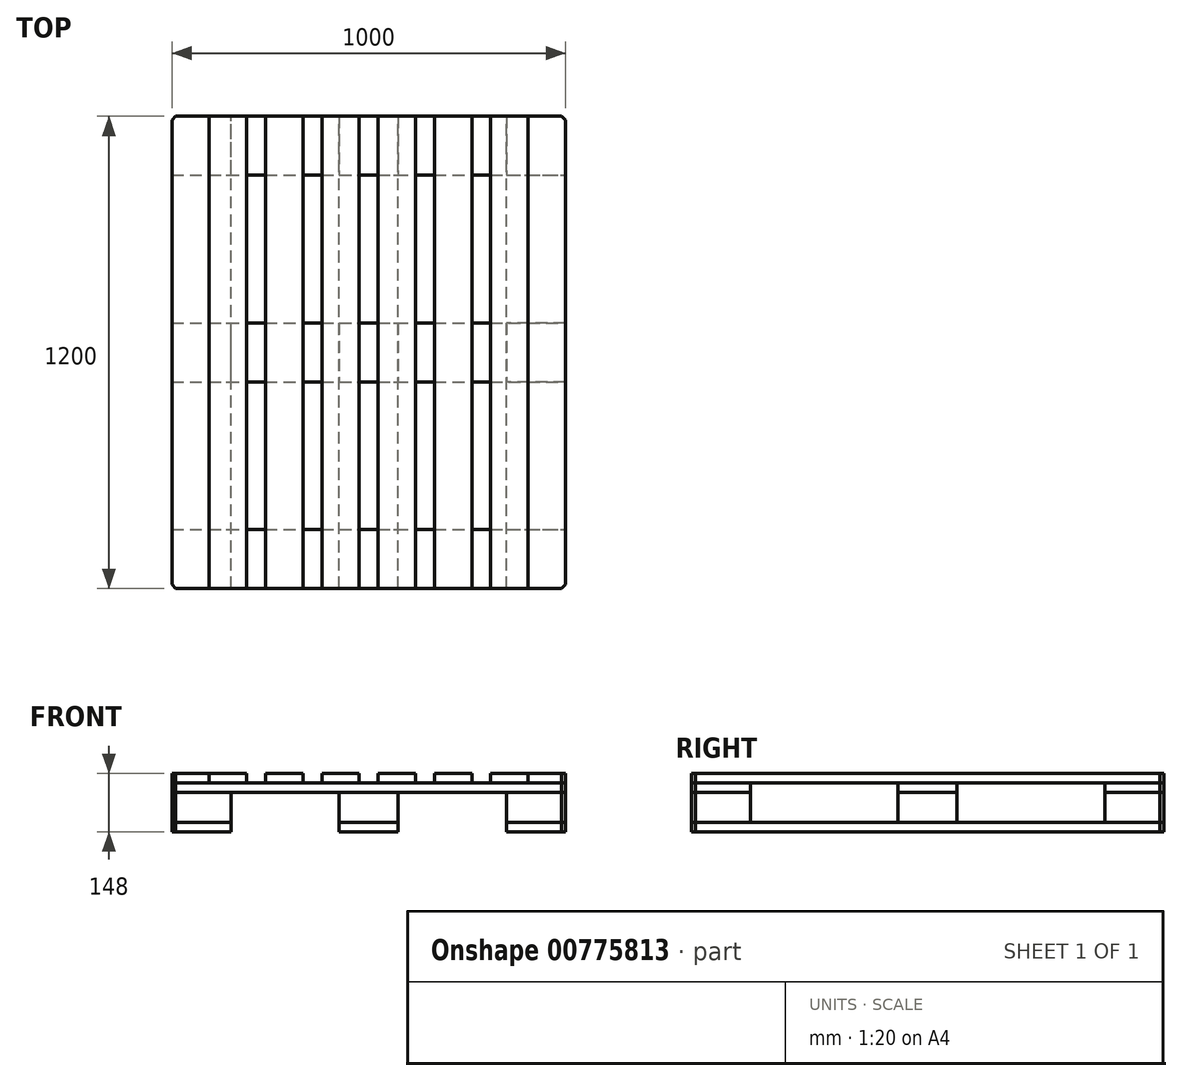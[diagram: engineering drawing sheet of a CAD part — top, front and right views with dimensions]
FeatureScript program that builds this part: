
annotation { "Feature Type Name" : "Feature", "Feature Type Description" : "" }
export const myFeature = defineFeature(function(context is Context, id is Id, definition is map)
    precondition{}
    {
        {
            var Q0;
            Q0=qCreatedBy(makeId("Top.planeOp"),FACE);
            var sketch = newSketch(context, id + "F0", { "sketchPlane" : qUnion([Q0])});
            skLineSegment(sketch, "E0.bottom", {"start": v(0, 0) * mm, "end": v(95, 0) * mm});
            skLineSegment(sketch, "E0.top", {"start": v(0, 1200) * mm, "end": v(95, 1200) * mm});
            skLineSegment(sketch, "E0.left", {"start": v(0, 0) * mm, "end": v(0, 1200) * mm});
            skLineSegment(sketch, "E0.right", {"start": v(95, 0) * mm, "end": v(95, 1200) * mm});
            skLineSegment(sketch, "E1.bottom", {"start": v(238, 0) * mm, "end": v(333, 0) * mm});
            skLineSegment(sketch, "E1.top", {"start": v(238, 1200) * mm, "end": v(333, 1200) * mm});
            skLineSegment(sketch, "E1.left", {"start": v(238, 0) * mm, "end": v(238, 1200) * mm});
            skLineSegment(sketch, "E1.right", {"start": v(333, 0) * mm, "end": v(333, 1200) * mm});
            skLineSegment(sketch, "E2.bottom", {"start": v(381, 0) * mm, "end": v(476, 0) * mm});
            skLineSegment(sketch, "E2.top", {"start": v(381, 1200) * mm, "end": v(476, 1200) * mm});
            skLineSegment(sketch, "E2.left", {"start": v(381, 0) * mm, "end": v(381, 1200) * mm});
            skLineSegment(sketch, "E2.right", {"start": v(476, 0) * mm, "end": v(476, 1200) * mm});
            skLineSegment(sketch, "E3.bottom", {"start": v(524, 0) * mm, "end": v(619, 0) * mm});
            skLineSegment(sketch, "E3.top", {"start": v(524, 1200) * mm, "end": v(619, 1200) * mm});
            skLineSegment(sketch, "E3.left", {"start": v(524, 0) * mm, "end": v(524, 1200) * mm});
            skLineSegment(sketch, "E3.right", {"start": v(619, 0) * mm, "end": v(619, 1200) * mm});
            skLineSegment(sketch, "E4.bottom", {"start": v(667, 0) * mm, "end": v(762, 0) * mm});
            skLineSegment(sketch, "E4.top", {"start": v(667, 1200) * mm, "end": v(762, 1200) * mm});
            skLineSegment(sketch, "E4.left", {"start": v(667, 0) * mm, "end": v(667, 1200) * mm});
            skLineSegment(sketch, "E4.right", {"start": v(762, 0) * mm, "end": v(762, 1200) * mm});
            skLineSegment(sketch, "E5.bottom", {"start": v(905, 0) * mm, "end": v(1000, 0) * mm});
            skLineSegment(sketch, "E5.top", {"start": v(905, 1200) * mm, "end": v(1000, 1200) * mm});
            skLineSegment(sketch, "E5.left", {"start": v(905, 0) * mm, "end": v(905, 1200) * mm});
            skLineSegment(sketch, "E5.right", {"start": v(1000, 0) * mm, "end": v(1000, 1200) * mm});
            skLineSegment(sketch, "E6.bottom", {"start": v(95.1, 0) * mm, "end": v(190, 0) * mm});
            skLineSegment(sketch, "E6.top", {"start": v(95.1, 1200) * mm, "end": v(190, 1200) * mm});
            skLineSegment(sketch, "E6.left", {"start": v(95.1, 0) * mm, "end": v(95.1, 1200) * mm});
            skLineSegment(sketch, "E6.right", {"start": v(190, 0) * mm, "end": v(190, 1200) * mm});
            skLineSegment(sketch, "E7.bottom", {"start": v(904.9, 0) * mm, "end": v(810, 0) * mm});
            skLineSegment(sketch, "E7.top", {"start": v(904.9, 1200) * mm, "end": v(810, 1200) * mm});
            skLineSegment(sketch, "E7.left", {"start": v(904.9, 0) * mm, "end": v(904.9, 1200) * mm});
            skLineSegment(sketch, "E7.right", {"start": v(810, 0) * mm, "end": v(810, 1200) * mm});
            skLineSegment(sketch, "E8", {"start": v(-393.77, 0) * mm, "end": v(-393.77, 800) * mm});
            skLineSegment(sketch, "E9", {"start": v(-393.77, 800) * mm, "end": v(1315.18, 800) * mm});
            skSolve(sketch);
        }
        {
            var Q0;
            Q0 = qSketchRegion(id + "F0", true);
            extrude(context, id + "F1", {"entities" : qUnion([Q0]), "depth" : 24 * mm, "offsetDistance" : 25 * mm});
        }
        {
            var Q0;
            Q0=qCreatedBy(makeId("Top.planeOp"),FACE);
            var sketch = newSketch(context, id + "F2", { "sketchPlane" : qUnion([Q0])});
            skLineSegment(sketch, "E10.bottom", {"start": v(0, 0) * mm, "end": v(1000, 0) * mm});
            skLineSegment(sketch, "E10.top", {"start": v(0, 150) * mm, "end": v(1000, 150) * mm});
            skLineSegment(sketch, "E10.left", {"start": v(0, 0) * mm, "end": v(0, 150) * mm});
            skLineSegment(sketch, "E10.right", {"start": v(1000, 0) * mm, "end": v(1000, 150) * mm});
            skLineSegment(sketch, "E11.bottom", {"start": v(0, 525) * mm, "end": v(1000, 525) * mm});
            skLineSegment(sketch, "E11.top", {"start": v(0, 675) * mm, "end": v(1000, 675) * mm});
            skLineSegment(sketch, "E11.left", {"start": v(0, 525) * mm, "end": v(0, 675) * mm});
            skLineSegment(sketch, "E11.right", {"start": v(1000, 525) * mm, "end": v(1000, 675) * mm});
            skLineSegment(sketch, "E12.bottom", {"start": v(0, 1050) * mm, "end": v(1000, 1050) * mm});
            skLineSegment(sketch, "E12.top", {"start": v(0, 1200) * mm, "end": v(1000, 1200) * mm});
            skLineSegment(sketch, "E12.left", {"start": v(0, 1050) * mm, "end": v(0, 1200) * mm});
            skLineSegment(sketch, "E12.right", {"start": v(1000, 1050) * mm, "end": v(1000, 1200) * mm});
            skSolve(sketch);
        }
        {
            var Q0;
            Q0 = qSketchRegion(id + "F2", true);
            extrude(context, id + "F3", {"entities" : qUnion([Q0]), "oppositeDirection" : true, "depth" : 24 * mm, "offsetDistance" : 25 * mm});
        }
        {
            var Q0;
            Q0=qCreatedBy(makeId("Top.planeOp"),FACE);
            var Q1;
            Q1 = qBodyType(qCreatedBy(id + "F5" ,EDGE), BodyType.WIRE);
            cPlane(context, id + "F4", {"entities" : qUnion([Q0, Q1]), "cplaneType" : CPlaneType.OFFSET, "offset" : 24 * mm, "oppositeDirection" : true, "width" : 150 * mm, "height" : 150 * mm});
        }
        {
            var Q0;
            Q0=qCreatedBy(id+"F4.planeOp",FACE);
            var sketch = newSketch(context, id + "F5", { "sketchPlane" : qUnion([Q0])});
            skLineSegment(sketch, "E13.bottom", {"start": v(0, 0) * mm, "end": v(150, 0) * mm});
            skLineSegment(sketch, "E13.top", {"start": v(0, 150) * mm, "end": v(150, 150) * mm});
            skLineSegment(sketch, "E13.left", {"start": v(0, 0) * mm, "end": v(0, 150) * mm});
            skLineSegment(sketch, "E13.right", {"start": v(150, 0) * mm, "end": v(150, 150) * mm});
            skLineSegment(sketch, "E14.bottom", {"start": v(0, 525) * mm, "end": v(150, 525) * mm});
            skLineSegment(sketch, "E14.top", {"start": v(0, 675) * mm, "end": v(150, 675) * mm});
            skLineSegment(sketch, "E14.left", {"start": v(0, 525) * mm, "end": v(0, 675) * mm});
            skLineSegment(sketch, "E14.right", {"start": v(150, 525) * mm, "end": v(150, 675) * mm});
            skLineSegment(sketch, "E15.bottom", {"start": v(0, 1050) * mm, "end": v(150, 1050) * mm});
            skLineSegment(sketch, "E15.top", {"start": v(0, 1200) * mm, "end": v(150, 1200) * mm});
            skLineSegment(sketch, "E15.left", {"start": v(0, 1050) * mm, "end": v(0, 1200) * mm});
            skLineSegment(sketch, "E15.right", {"start": v(150, 1050) * mm, "end": v(150, 1200) * mm});
            skLineSegment(sketch, "E16.bottom", {"start": v(425, 0) * mm, "end": v(575, 0) * mm});
            skLineSegment(sketch, "E16.top", {"start": v(425, 150) * mm, "end": v(575, 150) * mm});
            skLineSegment(sketch, "E16.left", {"start": v(425, 0) * mm, "end": v(425, 150) * mm});
            skLineSegment(sketch, "E16.right", {"start": v(575, 0) * mm, "end": v(575, 150) * mm});
            skLineSegment(sketch, "E17.bottom", {"start": v(425, 1200) * mm, "end": v(575, 1200) * mm});
            skLineSegment(sketch, "E17.top", {"start": v(425, 1050) * mm, "end": v(575, 1050) * mm});
            skLineSegment(sketch, "E17.left", {"start": v(425, 1200) * mm, "end": v(425, 1050) * mm});
            skLineSegment(sketch, "E17.right", {"start": v(575, 1200) * mm, "end": v(575, 1050) * mm});
            skLineSegment(sketch, "E18.bottom", {"start": v(850, 0) * mm, "end": v(1000, 0) * mm});
            skLineSegment(sketch, "E18.top", {"start": v(850, 150) * mm, "end": v(1000, 150) * mm});
            skLineSegment(sketch, "E18.left", {"start": v(850, 0) * mm, "end": v(850, 150) * mm});
            skLineSegment(sketch, "E18.right", {"start": v(1000, 0) * mm, "end": v(1000, 150) * mm});
            skLineSegment(sketch, "E19.bottom", {"start": v(850, 1200) * mm, "end": v(1000, 1200) * mm});
            skLineSegment(sketch, "E19.top", {"start": v(850, 1050) * mm, "end": v(1000, 1050) * mm});
            skLineSegment(sketch, "E19.left", {"start": v(850, 1200) * mm, "end": v(850, 1050) * mm});
            skLineSegment(sketch, "E19.right", {"start": v(1000, 1200) * mm, "end": v(1000, 1050) * mm});
            skLineSegment(sketch, "E20.bottom", {"start": v(1000, 675) * mm, "end": v(850, 675) * mm});
            skLineSegment(sketch, "E20.top", {"start": v(1000, 525) * mm, "end": v(850, 525) * mm});
            skLineSegment(sketch, "E20.left", {"start": v(1000, 675) * mm, "end": v(1000, 525) * mm});
            skLineSegment(sketch, "E20.right", {"start": v(850, 675) * mm, "end": v(850, 525) * mm});
            skLineSegment(sketch, "E21.bottom", {"start": v(425, 675) * mm, "end": v(575, 675) * mm});
            skLineSegment(sketch, "E21.top", {"start": v(425, 525) * mm, "end": v(575, 525) * mm});
            skLineSegment(sketch, "E21.left", {"start": v(425, 675) * mm, "end": v(425, 525) * mm});
            skLineSegment(sketch, "E21.right", {"start": v(575, 675) * mm, "end": v(575, 525) * mm});
            skSolve(sketch);
        }
        {
            var Q0;
            Q0 = qSketchRegion(id + "F5", true);
            extrude(context, id + "F6", {"entities" : qUnion([Q0]), "oppositeDirection" : true, "depth" : 76 * mm, "offsetDistance" : 25 * mm});
        }
        {
            var Q0;
            Q0=qCreatedBy(makeId("Top.planeOp"),FACE);
            cPlane(context, id + "F7", {"entities" : qUnion([Q0]), "cplaneType" : CPlaneType.OFFSET, "offset" : 100 * mm, "oppositeDirection" : true, "width" : 150 * mm, "height" : 150 * mm});
        }
        {
            var Q0;
            Q0=qCreatedBy(id+"F7.planeOp",FACE);
            var sketch = newSketch(context, id + "F8", { "sketchPlane" : qUnion([Q0])});
            skLineSegment(sketch, "E22.bottom", {"start": v(0, 0) * mm, "end": v(150, 0) * mm});
            skLineSegment(sketch, "E22.top", {"start": v(0, 1200) * mm, "end": v(150, 1200) * mm});
            skLineSegment(sketch, "E22.left", {"start": v(0, 0) * mm, "end": v(0, 1200) * mm});
            skLineSegment(sketch, "E22.right", {"start": v(150, 0) * mm, "end": v(150, 1200) * mm});
            skLineSegment(sketch, "E23.bottom", {"start": v(425, 0) * mm, "end": v(575, 0) * mm});
            skLineSegment(sketch, "E23.top", {"start": v(425, 1200) * mm, "end": v(575, 1200) * mm});
            skLineSegment(sketch, "E23.left", {"start": v(425, 0) * mm, "end": v(425, 1200) * mm});
            skLineSegment(sketch, "E23.right", {"start": v(575, 0) * mm, "end": v(575, 1200) * mm});
            skLineSegment(sketch, "E24.bottom", {"start": v(850, 0) * mm, "end": v(1000, 0) * mm});
            skLineSegment(sketch, "E24.top", {"start": v(850, 1200) * mm, "end": v(1000, 1200) * mm});
            skLineSegment(sketch, "E24.left", {"start": v(850, 0) * mm, "end": v(850, 1200) * mm});
            skLineSegment(sketch, "E24.right", {"start": v(1000, 0) * mm, "end": v(1000, 1200) * mm});
            skSolve(sketch);
        }
        {
            var Q0;
            Q0=makeQuery(id+"F8.imprint","IMPRINT",FACE,{"disambiguationData":[TD([[makeQuery(id+"F8.imprint","IMPRINT",EDGE,{"derivedFrom":sQuery(id+"F8.wireOp",EDGE,"EczPgE0n-K9yp-B3PO-EOS9-lX0zIsuZnhOC.bottom")}),1.0]])]});
            var Q1;
            Q1=makeQuery(id+"F8.imprint","IMPRINT",FACE,{"disambiguationData":[TD([[makeQuery(id+"F8.imprint","IMPRINT",EDGE,{"derivedFrom":sQuery(id+"F8.wireOp",EDGE,"n37sNpmZ-Vokc-glh2-zaN3-OXUCp4wZ9gNM.bottom")}),-1.0]])]});
            var Q2;
            Q2=makeQuery(id+"F8.imprint","IMPRINT",FACE,{"disambiguationData":[TD([[makeQuery(id+"F8.imprint","IMPRINT",EDGE,{"derivedFrom":sQuery(id+"F8.wireOp",EDGE,"Ks7QyBSp-k5Ov-2m7H-Jzkb-e3JOm2grHWz5.bottom")}),1.0]])]});
            var Q3;
            Q3=makeQuery(id+"F8.imprint","IMPRINT",FACE,{"disambiguationData":[TD([[makeQuery(id+"F8.imprint","IMPRINT",EDGE,{"derivedFrom":sQuery(id+"F8.wireOp",EDGE,"ck5NWcSz-vigR-tb6p-G7Lp-A0RWy0raUwrF.bottom")}),-1.0]])]});
            var Q4;
            Q4=makeQuery(id+"F8.imprint","IMPRINT",FACE,{"disambiguationData":[TD([[makeQuery(id+"F8.imprint","IMPRINT",EDGE,{"derivedFrom":sQuery(id+"F8.wireOp",EDGE,"sv6O0ENj-LKTy-FbcM-Dksy-kAM6wW1Upfch.bottom")}),1.0]])]});
            var Q5;
            Q5=makeQuery(id+"F8.imprint","IMPRINT",FACE,{"disambiguationData":[TD([[makeQuery(id+"F8.imprint","IMPRINT",EDGE,{"derivedFrom":sQuery(id+"F8.wireOp",EDGE,"OLO49vYj-GmuG-Gr7v-j1kl-gfgOTdw78I8l.bottom")}),-1.0]])]});
            var Q6;
            Q6=makeQuery(id+"F8.imprint","IMPRINT",FACE,{"disambiguationData":[TD([[makeQuery(id+"F8.imprint","IMPRINT",EDGE,{"derivedFrom":sQuery(id+"F8.wireOp",EDGE,"tdcu3QGg-uwbD-OHdg-jPnv-YvNIwUOHGk3V.bottom")}),1.0]])]});
            var Q7;
            Q7=makeQuery(id+"F8.imprint","IMPRINT",FACE,{"disambiguationData":[TD([[makeQuery(id+"F8.imprint","IMPRINT",EDGE,{"derivedFrom":sQuery(id+"F8.wireOp",EDGE,"E22.bottom")}),1.0]])]});
            var Q8;
            Q8=makeQuery(id+"F8.imprint","IMPRINT",FACE,{"disambiguationData":[TD([[makeQuery(id+"F8.imprint","IMPRINT",EDGE,{"derivedFrom":sQuery(id+"F8.wireOp",EDGE,"E23.bottom")}),1.0]])]});
            var Q9;
            Q9=makeQuery(id+"F8.imprint","IMPRINT",FACE,{"disambiguationData":[TD([[makeQuery(id+"F8.imprint","IMPRINT",EDGE,{"derivedFrom":sQuery(id+"F8.wireOp",EDGE,"E24.bottom")}),1.0]])]});
            extrude(context, id + "F9", {"entities" : qUnion([Q0, Q1, Q2, Q3, Q4, Q5, Q6, Q7, Q8, Q9]), "oppositeDirection" : true, "depth" : 24 * mm, "offsetDistance" : 25 * mm});
        }
        {
            var Q0;
            Q0=makeQuery(id+"F6.opExtrude","SWEPT_EDGE",EDGE,{"disambiguationData":[OSD([sQuery(id+"F5.wireOp",EDGE,"E13.bottom"),sQuery(id+"F5.wireOp",EDGE,"E13.left")])]});
            var Q1;
            Q1=makeQuery(id+"F3.opExtrude","SWEPT_EDGE",EDGE,{"disambiguationData":[OSD([sQuery(id+"F2.wireOp",EDGE,"E10.bottom"),sQuery(id+"F2.wireOp",EDGE,"E10.left")])]});
            var Q2;
            Q2=makeQuery(id+"F1.opExtrude","SWEPT_EDGE",EDGE,{"disambiguationData":[OSD([sQuery(id+"F0.wireOp",EDGE,"E0.bottom"),sQuery(id+"F0.wireOp",EDGE,"E0.left")])]});
            var Q3;
            Q3=makeQuery(id+"F9.opExtrude","SWEPT_EDGE",EDGE,{"disambiguationData":[OSD([sQuery(id+"F8.wireOp",EDGE,"E22.bottom"),sQuery(id+"F8.wireOp",EDGE,"E22.left")])]});
            var Q4;
            Q4=makeQuery(id+"F9.opExtrude","SWEPT_EDGE",EDGE,{"disambiguationData":[OSD([sQuery(id+"F8.wireOp",EDGE,"E24.bottom"),sQuery(id+"F8.wireOp",EDGE,"E24.right")])]});
            var Q5;
            Q5=makeQuery(id+"F6.opExtrude","SWEPT_EDGE",EDGE,{"disambiguationData":[OSD([sQuery(id+"F5.wireOp",EDGE,"E18.bottom"),sQuery(id+"F5.wireOp",EDGE,"E18.right")])]});
            var Q6;
            Q6=makeQuery(id+"F3.opExtrude","SWEPT_EDGE",EDGE,{"disambiguationData":[OSD([sQuery(id+"F2.wireOp",EDGE,"E10.bottom"),sQuery(id+"F2.wireOp",EDGE,"E10.right")])]});
            var Q7;
            Q7=makeQuery(id+"F1.opExtrude","SWEPT_EDGE",EDGE,{"disambiguationData":[OSD([sQuery(id+"F0.wireOp",EDGE,"E5.bottom"),sQuery(id+"F0.wireOp",EDGE,"E5.right")])]});
            var Q8;
            Q8=makeQuery(id+"F1.opExtrude","SWEPT_EDGE",EDGE,{"disambiguationData":[OSD([sQuery(id+"F0.wireOp",EDGE,"E5.top"),sQuery(id+"F0.wireOp",EDGE,"E5.right")])]});
            var Q9;
            Q9=makeQuery(id+"F3.opExtrude","SWEPT_EDGE",EDGE,{"disambiguationData":[OSD([sQuery(id+"F2.wireOp",EDGE,"E12.top"),sQuery(id+"F2.wireOp",EDGE,"E12.right")])]});
            var Q10;
            Q10=makeQuery(id+"F6.opExtrude","SWEPT_EDGE",EDGE,{"disambiguationData":[OSD([sQuery(id+"F5.wireOp",EDGE,"E19.bottom"),sQuery(id+"F5.wireOp",EDGE,"E19.right")])]});
            var Q11;
            Q11=makeQuery(id+"F9.opExtrude","SWEPT_EDGE",EDGE,{"disambiguationData":[OSD([sQuery(id+"F8.wireOp",EDGE,"E24.top"),sQuery(id+"F8.wireOp",EDGE,"E24.right")])]});
            var Q12;
            Q12=makeQuery(id+"F1.opExtrude","SWEPT_EDGE",EDGE,{"disambiguationData":[OSD([sQuery(id+"F0.wireOp",EDGE,"E0.top"),sQuery(id+"F0.wireOp",EDGE,"E0.left")])]});
            var Q13;
            Q13=makeQuery(id+"F3.opExtrude","SWEPT_EDGE",EDGE,{"disambiguationData":[OSD([sQuery(id+"F2.wireOp",EDGE,"E12.top"),sQuery(id+"F2.wireOp",EDGE,"E12.left")])]});
            var Q14;
            Q14=makeQuery(id+"F6.opExtrude","SWEPT_EDGE",EDGE,{"disambiguationData":[OSD([sQuery(id+"F5.wireOp",EDGE,"E15.top"),sQuery(id+"F5.wireOp",EDGE,"E15.left")])]});
            var Q15;
            Q15=makeQuery(id+"F9.opExtrude","SWEPT_EDGE",EDGE,{"disambiguationData":[OSD([sQuery(id+"F8.wireOp",EDGE,"E22.top"),sQuery(id+"F8.wireOp",EDGE,"E22.left")])]});
            chamfer(context, id + "F10", {"entities" : qUnion([Q0, Q1, Q2, Q3, Q4, Q5, Q6, Q7, Q8, Q9, Q10, Q11, Q12, Q13, Q14, Q15]), "width" : 10 * mm, "tangentPropagation" : true});
        }
    });
